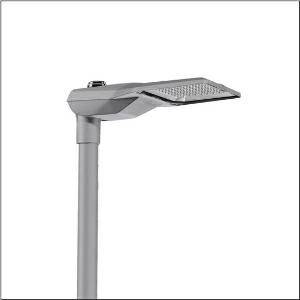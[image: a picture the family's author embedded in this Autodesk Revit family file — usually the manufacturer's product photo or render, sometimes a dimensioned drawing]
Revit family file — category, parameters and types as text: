
# Revit family: streetlight_sl_21_midi___pl52_5xe7h37n08mb_03fc
name_source: partatom
category: Lighting Fixtures
units: mm (PartAtom-declared; Revit-internal decimal feet)

## family parameters
Cut with Voids When Loaded = No
Host = Face
Light Source = No
Part Type = Normal
Room Calculation Point = No
Round Connector Dimension = Use Diameter
Shared = No

## types (1)
- --- (1 x LED, 17960 lm, 136 W, 3000K)
    Apparent Load = 136 VA
    CIE Flux Codes = 27 59 98 100 100
    Color Rendering = 70
    Color Temperature = 3000K
    Default Elevation = 1800 mm
    Description = Streetlight SL 21 midi, mast luminaire, primary light control with lens, of PMMA, primary optical cover: cover, of toughened safety glass, transparent, light distribution: PL52, light emission: direct distribution, primary light characteristic: asymmetric, installation type: side-entry, LED, 3G 2.5mm², High Power LED, rated luminous flux: 17.960lm, luminous efficacy: 132lm/W, light colour: 730, colour temperature: 3000K, control: overheat protection, presetting dimming linear, constant luminous flux control, time-dependent luminous flux control, flexible luminous flux parameterisation, mains connection: 220..240V, AC, 50/60Hz, connection cable pre-assembled, cable length: 12,5m, wiring characteristics: H05VV-F, start of lifetime: 136W, end of service life: 142W, reduction: 61W, luminaire housing, of diecast aluminium (EN AC-44300), powder-coated, Siteco® metallic grey (DB 702S), corrosivity category C5 mid according to DIN EN ISO 12944, multi-level sealing system, sealing non-destructively replaceable, inclination adjustable: 0°, 5°, 10°, 15°, length: 644mm, width: 335mm, height: 110mm, spigot size: 42mm (side-entry), protection rating (complete): IP66, insulation class (complete): insulation class I (protective earthing), certification: CE, ENEC, ENEC+, VDE, impact resistance: IK09, permissible operating ambient temperature for outdoor applications: -40..+50°C, standard-compliant lighting for roads and squares, packaging unit: 1 piece

Light Distribution: PL52
    Height = 111 mm
    Lamp = 1 x LED
    Lamp Light Flux = 17960 lm
    Lamp Power = 136 W
    Lamp count = 1
    Length = 644 mm
    Luminous efficacy = 132 lm/W
    Manufacturer = Siteco
    ModVariant = No
    Model = 5XE7H37N08MB
    Number of Poles = 1
    OnlyDefault = Yes
    Power Factor = 1
    Product Name = Streetlight SL 21 midi | PL52
    Product group = mast luminaire | pylon top
    ProductGroupID = 6100
    Protection Class = Protection class I
    Protection Degree = IP 66
    RLX_Detail_Level = 1
    RLX_Emergency_Light_Flux = 0 lm
    RLX_Emergency_Type = 0
    RLX_Emergency_Type_DB = No
    RlxData = <blob elided: 99873 chars, md5=609afa3b>
    Socket = socket
    Standby Power = 0 W
    System Light Flux = 17960 lm
    System Power = 136 W
    Type Comments = factory setting: luminous flux: 100 % | dim-lin: 254 | 695 mA
    Type Image = l_1294377.jpg
    URL = http://relux.com
    VarID = @adj_086265
    Voltage = 0 V
    Weight = 0.00 kg
    Width = 336 mm

## geometry (parser evidence)
native form markers: Blend x4, Sweep x13
no freeform markers — native parametric forms only
